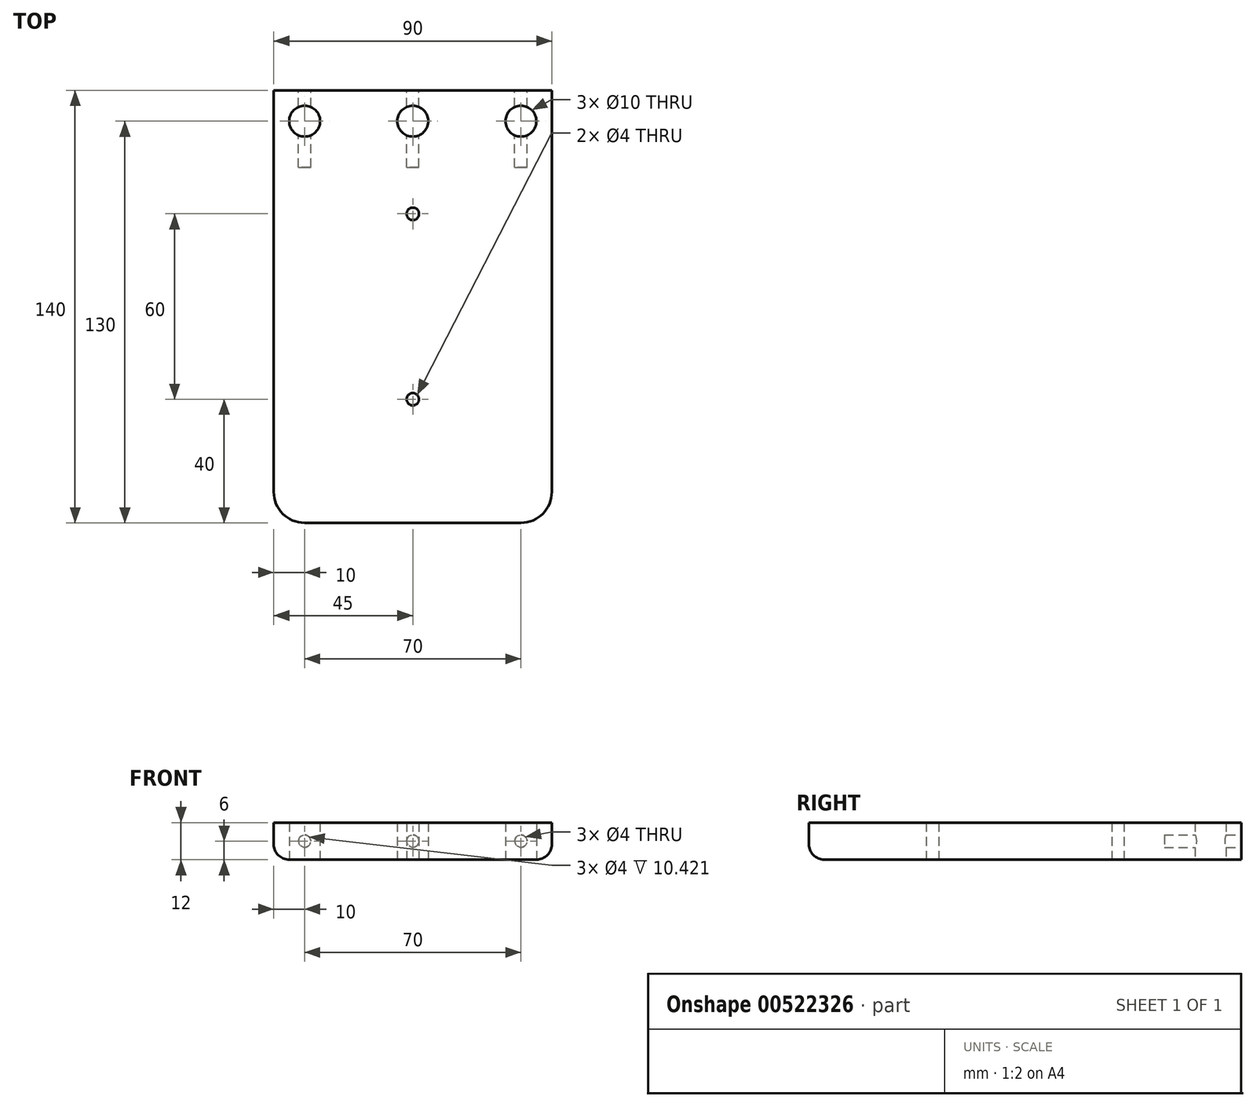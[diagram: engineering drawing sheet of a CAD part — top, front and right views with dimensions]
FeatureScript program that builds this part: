
annotation { "Feature Type Name" : "Feature", "Feature Type Description" : "" }
export const myFeature = defineFeature(function(context is Context, id is Id, definition is map)
    precondition{}
    {
        {
            var Q0;
            Q0=qCreatedBy(makeId("Top.planeOp"),FACE);
            var sketch = newSketch(context, id + "F0", { "sketchPlane" : qUnion([Q0])});
            skLineSegment(sketch, "E0.bottom", {"start": v(35, -70) * mm, "end": v(-35, -70) * mm});
            skLineSegment(sketch, "E0.top", {"start": v(45, 70) * mm, "end": v(-45, 70) * mm});
            skLineSegment(sketch, "E0.left", {"start": v(45, -60) * mm, "end": v(45, 70) * mm});
            skLineSegment(sketch, "E0.right", {"start": v(-45, -60) * mm, "end": v(-45, 70) * mm});
            skPoint(sketch, "E0.middle", {"position": v(0, 0) * mm});
            skPoint(sketch, "E1.visualSharp", {"position": v(-45, -70) * mm});
            skArc(sketch, "E1.filletArc", {"start": v(-45, -60) * mm, "mid": v(-42.07, -67.07) * mm, "end": v(-35, -70) * mm});
            skPoint(sketch, "E2.visualSharp", {"position": v(45, -70) * mm});
            skArc(sketch, "E2.filletArc", {"start": v(35, -70) * mm, "mid": v(42.07, -67.07) * mm, "end": v(45, -60) * mm});
            skCircle(sketch, "E3", {"center": v(0, 60) * mm, "radius": 5 * mm});
            skPoint(sketch, "E3.centerSnap0", {"position": v(0, 70) * mm});
            skCircle(sketch, "E4", {"center": v(35, 60) * mm, "radius": 5 * mm});
            skCircle(sketch, "E5", {"center": v(-35, 60) * mm, "radius": 5 * mm});
            skCircle(sketch, "E6", {"center": v(0, 30) * mm, "radius": 2 * mm});
            skCircle(sketch, "E7", {"center": v(0, -30) * mm, "radius": 2 * mm});
            skSolve(sketch);
        }
        {
            var Q0;
            Q0=makeQuery(id+"F0.imprint","IMPRINT",FACE,{"disambiguationData":[TD([[makeQuery(id+"F0.imprint","IMPRINT",EDGE,{"derivedFrom":sQuery(id+"F0.wireOp",EDGE,"E0.bottom")}),-1.0]])]});
            extrude(context, id + "F1", {"entities" : qUnion([Q0]), "depth" : 12 * mm, "offsetDistance" : 25 * mm});
        }
        {
            var Q0;
            Q0=makeQuery(id+"F1.opExtrude","SWEPT_FACE",FACE,{"disambiguationData":[OSD([sQuery(id+"F0.wireOp",EDGE,"E0.top")])]});
            var sketch = newSketch(context, id + "F2", { "sketchPlane" : qUnion([Q0])});
            skCircle(sketch, "E8", {"center": v(0, 6) * mm, "radius": 2 * mm});
            skPoint(sketch, "E8.centerSnap0", {"position": v(-45, 6) * mm});
            skCircle(sketch, "E9", {"center": v(35, 6) * mm, "radius": 2 * mm});
            skCircle(sketch, "E10", {"center": v(-35, 6) * mm, "radius": 2 * mm});
            skSolve(sketch);
        }
        {
            var Q0;
            Q0 = qSketchRegion(id + "F2", true);
            extrude(context, id + "F3", {"entities" : qUnion([Q0]), "operationType" : NewBodyOperationType.REMOVE, "oppositeDirection" : true, "depth" : 25 * mm, "offsetDistance" : 25 * mm});
        }
        {
            var Q0;
            Q0=makeQuery(id+"F1.opExtrude","CAP_EDGE",EDGE,{"disambiguationData":[OSD([sQuery(id+"F0.wireOp",EDGE,"E0.left")])],"isStart":true});
            fillet(context, id + "F4", {"entities" : qUnion([Q0]), "radius" : 5 * mm, "tangentPropagation" : true, "allowEdgeOverflow" : false});
        }
    });
